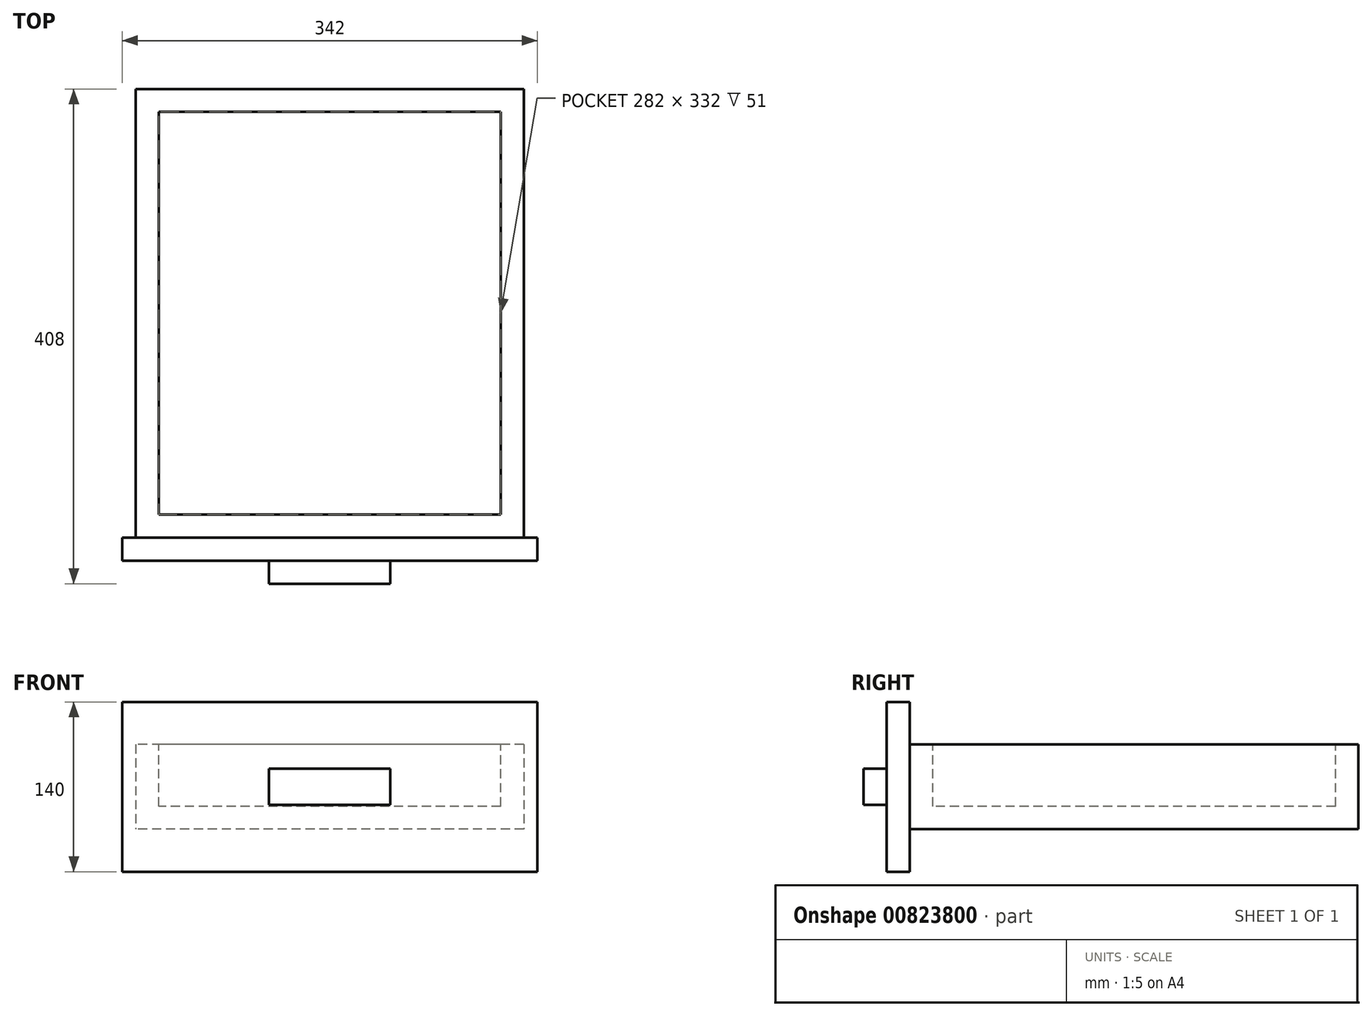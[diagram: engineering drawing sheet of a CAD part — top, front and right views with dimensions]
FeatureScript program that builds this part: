
annotation { "Feature Type Name" : "Feature", "Feature Type Description" : "" }
export const myFeature = defineFeature(function(context is Context, id is Id, definition is map)
    precondition{}
    {
        {
            var Q0;
            Q0=qCreatedBy(makeId("Top.planeOp"),FACE);
            var sketch = newSketch(context, id + "F0", { "sketchPlane" : qUnion([Q0])});
            skLineSegment(sketch, "E0.bottom", {"start": v(160, -185) * mm, "end": v(-160, -185) * mm});
            skLineSegment(sketch, "E0.top", {"start": v(160, 185) * mm, "end": v(-160, 185) * mm});
            skLineSegment(sketch, "E0.left", {"start": v(160, -185) * mm, "end": v(160, 185) * mm});
            skLineSegment(sketch, "E0.right", {"start": v(-160, -185) * mm, "end": v(-160, 185) * mm});
            skPoint(sketch, "E0.middle", {"position": v(0, 0) * mm});
            skSolve(sketch);
        }
        {
            var Q0;
            Q0 = qSketchRegion(id + "F0", true);
            extrude(context, id + "F1", {"entities" : qUnion([Q0]), "depth" : 70 * mm, "offsetDistance" : 25 * mm});
        }
        {
            var Q0;
            Q0=makeQuery(id+"F1.opExtrude","CAP_FACE",FACE,{"disambiguationData":[OSD([sQuery(id+"F0.wireOp",EDGE,"E0.bottom"),sQuery(id+"F0.wireOp",EDGE,"E0.top"),sQuery(id+"F0.wireOp",EDGE,"E0.left"),sQuery(id+"F0.wireOp",EDGE,"E0.right")])],"isStart":false});
            var sketch = newSketch(context, id + "F2", { "sketchPlane" : qUnion([Q0])});
            skLineSegment(sketch, "E1.bottom", {"start": v(141, 166) * mm, "end": v(-141, 166) * mm});
            skLineSegment(sketch, "E1.top", {"start": v(141, -166) * mm, "end": v(-141, -166) * mm});
            skLineSegment(sketch, "E1.left", {"start": v(141, 166) * mm, "end": v(141, -166) * mm});
            skLineSegment(sketch, "E1.right", {"start": v(-141, 166) * mm, "end": v(-141, -166) * mm});
            skPoint(sketch, "E1.middle", {"position": v(0, 0) * mm});
            skSolve(sketch);
        }
        {
            var Q0;
            Q0=makeQuery(id+"F2.imprint","IMPRINT",FACE,{"disambiguationData":[TD([[makeQuery(id+"F2.imprint","IMPRINT",EDGE,{"derivedFrom":sQuery(id+"F2.wireOp",EDGE,"E1.bottom")}),1.0]])]});
            extrude(context, id + "F3", {"entities" : qUnion([Q0]), "operationType" : NewBodyOperationType.REMOVE, "oppositeDirection" : true, "depth" : 51 * mm, "offsetDistance" : 25 * mm});
        }
        {
            var Q0;
            Q0=makeQuery(id+"F1.opExtrude","SWEPT_FACE",FACE,{"disambiguationData":[OSD([sQuery(id+"F0.wireOp",EDGE,"E0.bottom")])]});
            var sketch = newSketch(context, id + "F4", { "sketchPlane" : qUnion([Q0])});
            skLineSegment(sketch, "E2.bottom", {"start": v(171, 105) * mm, "end": v(-171, 105) * mm});
            skLineSegment(sketch, "E2.top", {"start": v(171, -35) * mm, "end": v(-171, -35) * mm});
            skLineSegment(sketch, "E2.left", {"start": v(171, 105) * mm, "end": v(171, -35) * mm});
            skLineSegment(sketch, "E2.right", {"start": v(-171, 105) * mm, "end": v(-171, -35) * mm});
            skPoint(sketch, "E2.middle", {"position": v(0, 35) * mm});
            skPoint(sketch, "E2.middle.positionSnap0", {"position": v(-160, 35) * mm});
            skPoint(sketch, "E2.middle.positionSnap1", {"position": v(0, 0) * mm});
            skPoint(sketch, "E2.centerSnap0", {"position": v(-160, 35) * mm});
            skPoint(sketch, "E2.centerSnap1", {"position": v(0, 0) * mm});
            skSolve(sketch);
        }
        {
            var Q0;
            {var subQ0=sQuery(id+"F0.wireOp",EDGE,"E0.bottom");Q0=makeQuery(id+"F4.imprint","IMPRINT",FACE,{"disambiguationData":[TD([[makeQuery(id+"F4.imprint","IMPRINT",EDGE,{"derivedFrom":makeQuery(id+"F1.opExtrude","CAP_EDGE",EDGE,{"disambiguationData":[OSD([subQ0])],"isStart":true})}),-1.0]])]});}
            var Q1;
            Q1=makeQuery(id+"F4.imprint","IMPRINT",FACE,{"disambiguationData":[TD([[makeQuery(id+"F4.imprint","IMPRINT",EDGE,{"derivedFrom":sQuery(id+"F4.wireOp",EDGE,"E2.bottom")}),1.0]])]});
            extrude(context, id + "F5", {"entities" : qUnion([Q0, Q1]), "operationType" : NewBodyOperationType.ADD, "depth" : 19 * mm, "offsetDistance" : 25 * mm});
        }
        {
            var Q0;
            Q0=makeQuery(id+"F5.opExtrude","CAP_FACE",FACE,{"disambiguationData":[OSD([sQuery(id+"F4.wireOp",EDGE,"E2.bottom"),sQuery(id+"F4.wireOp",EDGE,"E2.top"),sQuery(id+"F4.wireOp",EDGE,"E2.left"),sQuery(id+"F4.wireOp",EDGE,"E2.right")])],"isStart":false});
            var sketch = newSketch(context, id + "F6", { "sketchPlane" : qUnion([Q0])});
            skLineSegment(sketch, "E3.bottom", {"start": v(50, 20) * mm, "end": v(-50, 20) * mm});
            skLineSegment(sketch, "E3.top", {"start": v(50, 50) * mm, "end": v(-50, 50) * mm});
            skLineSegment(sketch, "E3.left", {"start": v(50, 20) * mm, "end": v(50, 50) * mm});
            skLineSegment(sketch, "E3.right", {"start": v(-50, 20) * mm, "end": v(-50, 50) * mm});
            skPoint(sketch, "E3.middle", {"position": v(0, 35) * mm});
            skPoint(sketch, "E3.middle.positionSnap0", {"position": v(171, 35) * mm});
            skPoint(sketch, "E3.centerSnap0", {"position": v(171, 35) * mm});
            skSolve(sketch);
        }
        {
            var Q0;
            Q0=makeQuery(id+"F6.imprint","IMPRINT",FACE,{"disambiguationData":[TD([[makeQuery(id+"F6.imprint","IMPRINT",EDGE,{"derivedFrom":sQuery(id+"F6.wireOp",EDGE,"E3.bottom")}),-1.0]])]});
            extrude(context, id + "F7", {"entities" : qUnion([Q0]), "operationType" : NewBodyOperationType.ADD, "depth" : 19 * mm, "offsetDistance" : 25 * mm});
        }
    });
